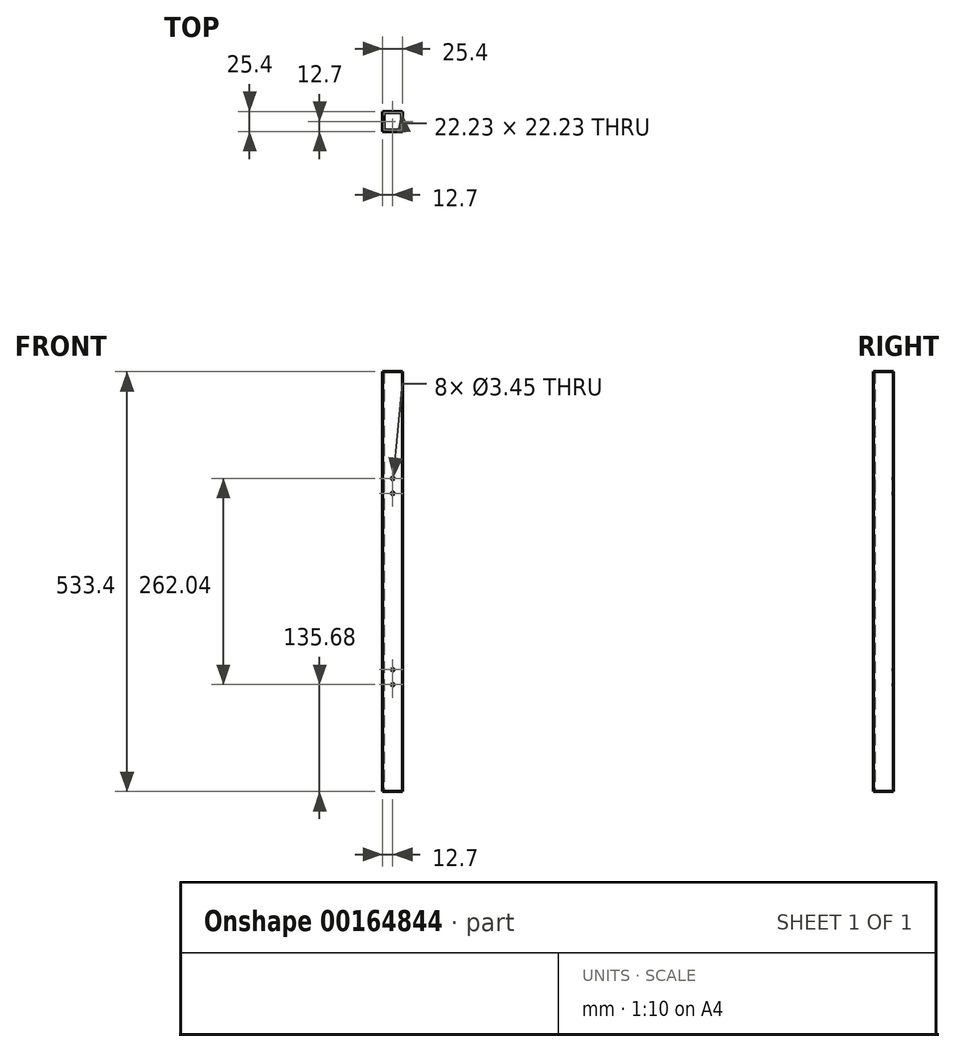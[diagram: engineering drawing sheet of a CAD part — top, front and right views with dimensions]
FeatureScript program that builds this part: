
annotation { "Feature Type Name" : "Feature", "Feature Type Description" : "" }
export const myFeature = defineFeature(function(context is Context, id is Id, definition is map)
    precondition{}
    {
        {
            var Q0;
            Q0=qCreatedBy(makeId("Top.planeOp"),FACE);
            var sketch = newSketch(context, id + "F0", { "sketchPlane" : qUnion([Q0])});
            skLineSegment(sketch, "E0.bottom", {"start": v(11.11, -11.11) * mm, "end": v(-11.11, -11.11) * mm});
            skLineSegment(sketch, "E0.top", {"start": v(11.11, 11.11) * mm, "end": v(-11.11, 11.11) * mm});
            skLineSegment(sketch, "E0.left", {"start": v(11.11, -11.11) * mm, "end": v(11.11, 11.11) * mm});
            skLineSegment(sketch, "E0.right", {"start": v(-11.11, -11.11) * mm, "end": v(-11.11, 11.11) * mm});
            skPoint(sketch, "E0.middle", {"position": v(0, 0) * mm});
            skLineSegment(sketch, "E1.bottom", {"start": v(12.7, -12.7) * mm, "end": v(-12.7, -12.7) * mm});
            skLineSegment(sketch, "E1.top", {"start": v(12.7, 12.7) * mm, "end": v(-12.7, 12.7) * mm});
            skLineSegment(sketch, "E1.left", {"start": v(12.7, -12.7) * mm, "end": v(12.7, 12.7) * mm});
            skLineSegment(sketch, "E1.right", {"start": v(-12.7, -12.7) * mm, "end": v(-12.7, 12.7) * mm});
            skSolve(sketch);
        }
        {
            var Q0;
            Q0 = qSketchRegion(id + "F0", true);
            extrude(context, id + "F1", {"entities" : qUnion([Q0]), "depth" : 533.4 * mm});
        }
        {
            var Q0;
            Q0=makeQuery(id+"F1.opExtrude","SWEPT_FACE",FACE,{"disambiguationData":[OSD([sQuery(id+"F0.wireOp",EDGE,"E1.bottom")])]});
            var sketch = newSketch(context, id + "F2", { "sketchPlane" : qUnion([Q0])});
            skLineSegment(sketch, "E2", {"start": v(0, 0) * mm, "end": v(0, 135.68) * mm, "construction": true});
            skLineSegment(sketch, "E3", {"start": v(0, 135.68) * mm, "end": v(0, 154.73) * mm, "construction": true});
            skLineSegment(sketch, "E4", {"start": v(0, 533.4) * mm, "end": v(0, 397.72) * mm, "construction": true});
            skLineSegment(sketch, "E5", {"start": v(0, 397.72) * mm, "end": v(0, 378.67) * mm, "construction": true});
            skCircle(sketch, "E6", {"center": v(0, 135.68) * mm, "radius": 1.73 * mm});
            skCircle(sketch, "E7", {"center": v(0, 154.73) * mm, "radius": 1.73 * mm});
            skCircle(sketch, "E8", {"center": v(0, 397.72) * mm, "radius": 1.73 * mm});
            skCircle(sketch, "E9", {"center": v(0, 378.67) * mm, "radius": 1.73 * mm});
            skSolve(sketch);
        }
        {
            var Q0;
            Q0 = qSketchRegion(id + "F2", true);
            var Q1;
            Q1=makeQuery(id+"F1.opExtrude","SWEPT_FACE",FACE,{"disambiguationData":[OSD([sQuery(id+"F0.wireOp",EDGE,"E1.top")])]});
            extrude(context, id + "F3", {"entities" : qUnion([Q0]), "operationType" : NewBodyOperationType.REMOVE, "endBound" : BoundingType.UP_TO_SURFACE, "oppositeDirection" : true, "endBoundEntityFace" : qUnion([Q1]), "depth" : 25.4 * mm});
        }
    });
